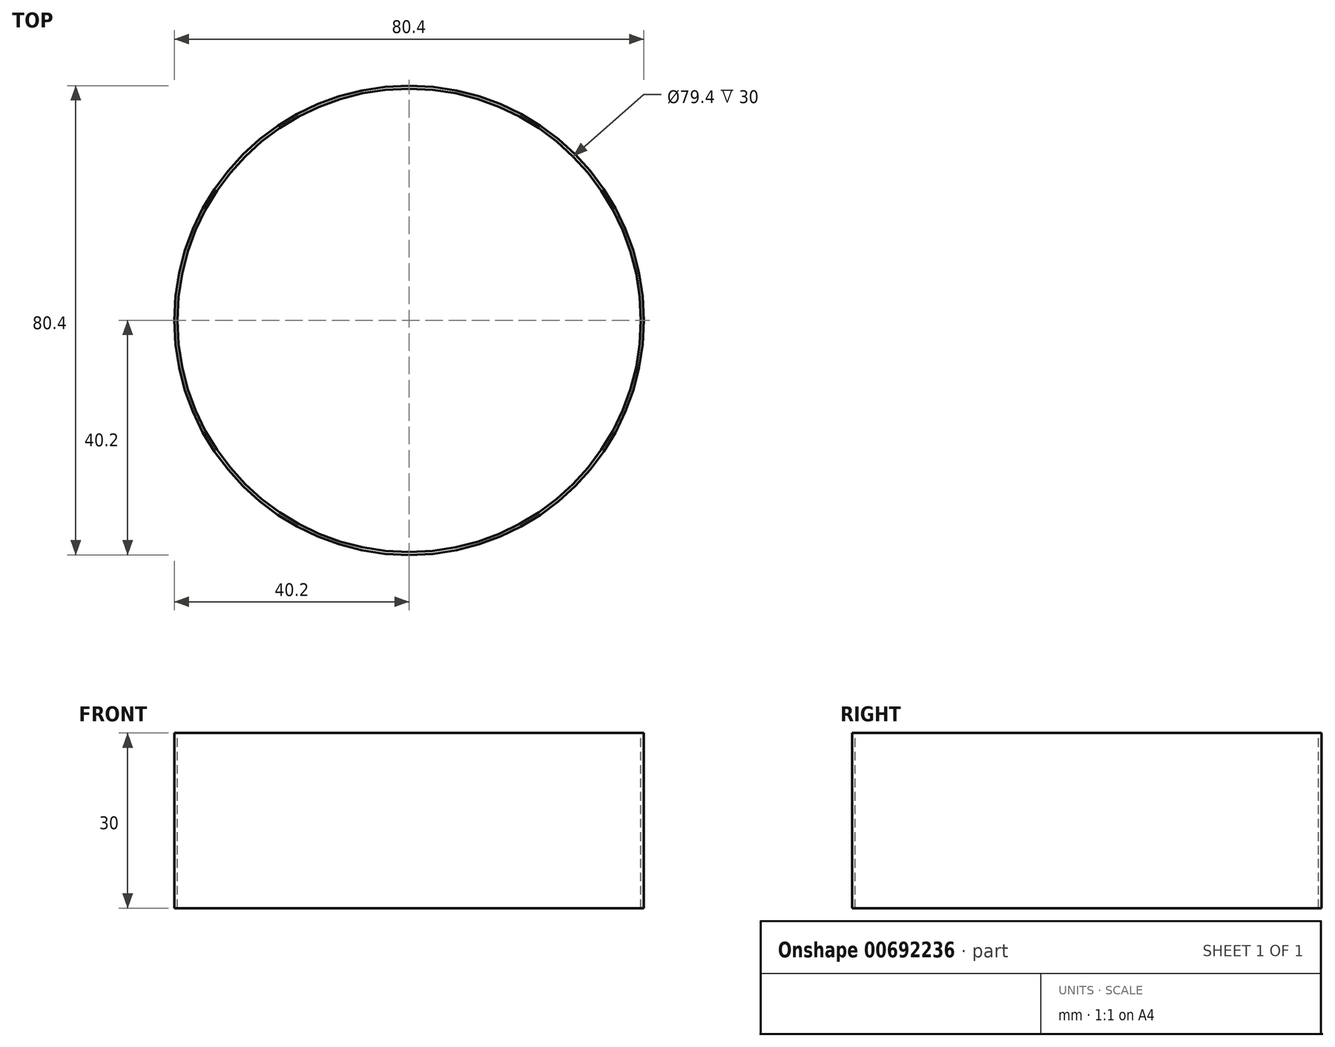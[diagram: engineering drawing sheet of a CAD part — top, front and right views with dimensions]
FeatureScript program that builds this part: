
annotation { "Feature Type Name" : "Feature", "Feature Type Description" : "" }
export const myFeature = defineFeature(function(context is Context, id is Id, definition is map)
    precondition{}
    {
        {
            var Q0;
            Q0=qCreatedBy(makeId("Front.planeOp"),FACE);
            var sketch = newSketch(context, id + "F0", { "sketchPlane" : qUnion([Q0])});
            skLineSegment(sketch, "E0", {"start": v(-40.2, 30) * mm, "end": v(-40.2, 0) * mm});
            skLineSegment(sketch, "E1", {"start": v(-39.7, 0) * mm, "end": v(-39.7, 30) * mm});
            skLineSegment(sketch, "E2", {"start": v(-39.7, 30) * mm, "end": v(-40.2, 30) * mm});
            skLineSegment(sketch, "E3", {"start": v(-39.7, 0) * mm, "end": v(-40.2, 0) * mm});
            skLineSegment(sketch, "E4", {"start": v(0, 0) * mm, "end": v(0, -12.3) * mm});
            skSolve(sketch);
        }
        {
            var Q0;
            Q0=qSketchRegion(id+"F0",true);
            var Q1;
            Q1=sQuery(id+"F0.wireOp",EDGE,"E4");
            revolve(context, id + "F1", {"surfaceOperationType" : NewSurfaceOperationType.NEW, "entities" : qUnion([Q0]), "axis" : qUnion([Q1]), "revolveType" : RevolveType.FULL});
        }
    });
